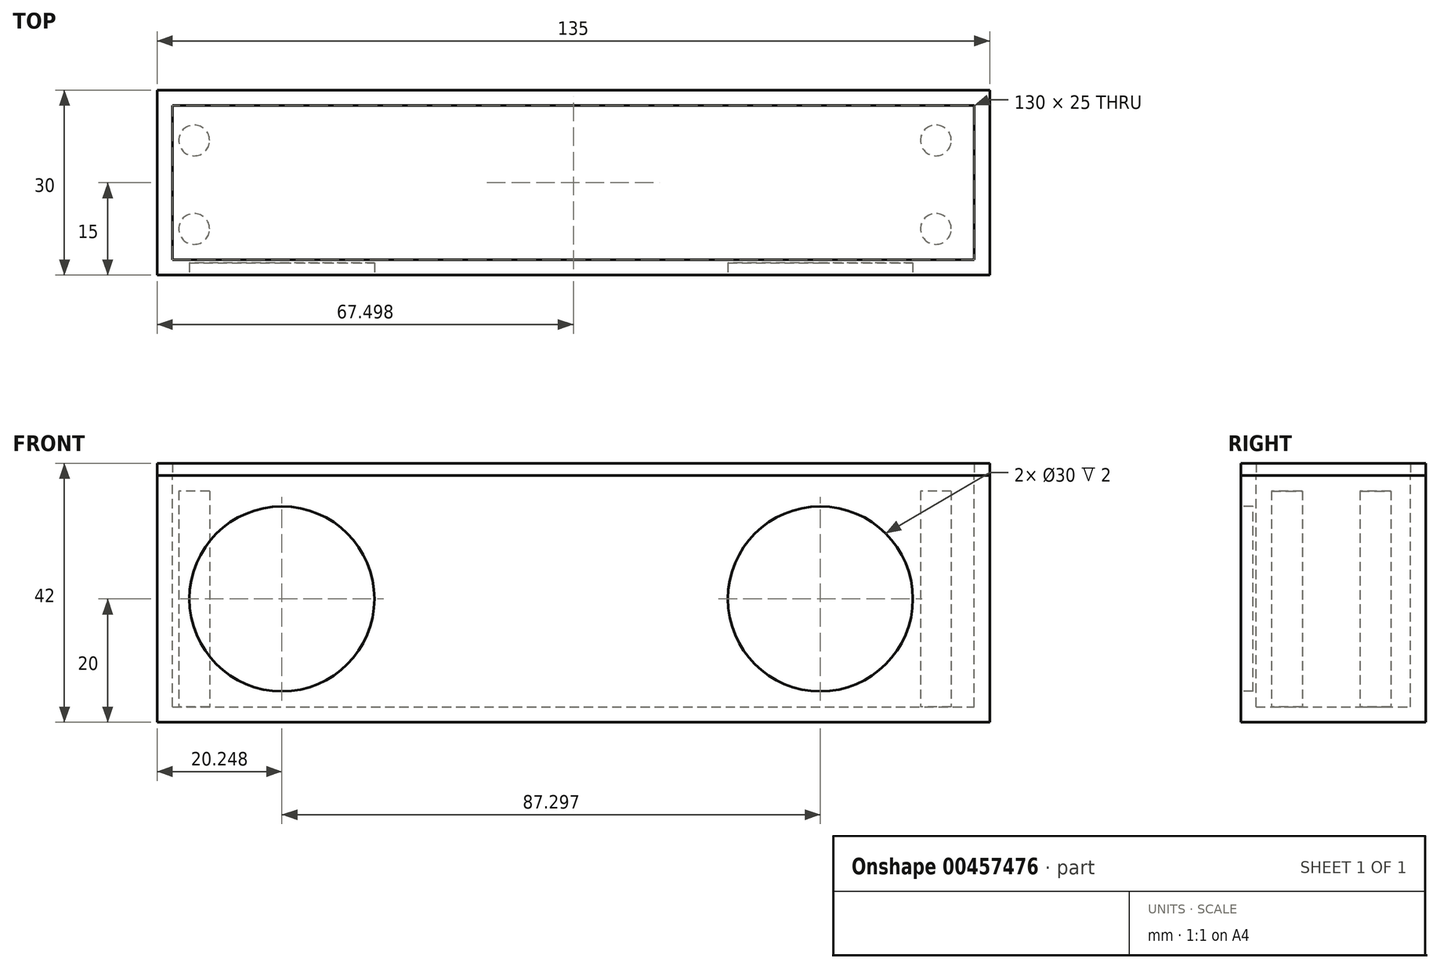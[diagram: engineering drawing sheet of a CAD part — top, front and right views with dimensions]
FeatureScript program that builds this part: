
annotation { "Feature Type Name" : "Feature", "Feature Type Description" : "" }
export const myFeature = defineFeature(function(context is Context, id is Id, definition is map)
    precondition{}
    {
        {
            var Q0;
            Q0=qCreatedBy(makeId("Front.planeOp"),FACE);
            var sketch = newSketch(context, id + "F0", { "sketchPlane" : qUnion([Q0])});
            skLineSegment(sketch, "E0.bottom", {"start": v(-68.08, 0) * mm, "end": v(66.92, 0) * mm});
            skLineSegment(sketch, "E0.top", {"start": v(-68.08, 30) * mm, "end": v(66.92, 30) * mm});
            skLineSegment(sketch, "E0.left", {"start": v(-68.08, 0) * mm, "end": v(-68.08, 30) * mm});
            skLineSegment(sketch, "E0.right", {"start": v(66.92, 0) * mm, "end": v(66.92, 30) * mm});
            skSolve(sketch);
        }
        {
            var Q0;
            Q0=makeQuery(id+"F0.imprint","IMPRINT",FACE,{"disambiguationData":[TD([[makeQuery(id+"F0.imprint","IMPRINT",EDGE,{"derivedFrom":sQuery(id+"F0.wireOp",EDGE,"E0.bottom")}),1.0]])]});
            extrude(context, id + "F1", {"entities" : qUnion([Q0]), "depth" : 30 * mm});
        }
        {
            var Q0;
            Q0=makeQuery(id+"F1.opExtrude","SWEPT_FACE",FACE,{"disambiguationData":[OSD([sQuery(id+"F0.wireOp",EDGE,"E0.top")])]});
            shell(context, id + "F2", {"entities" : qUnion([Q0]), "thickness" : 2.5 * mm});
        }
        {
            var Q0;
            Q0=makeQuery(id+"F2.opShell","OFFSET_FACE",FACE,{"disambiguationData":[OSD([sQuery(id+"F0.wireOp",EDGE,"E0.bottom")])]});
            var sketch = newSketch(context, id + "F3", { "sketchPlane" : qUnion([Q0])});
            skCircle(sketch, "E1", {"center": v(-62.07, -8.15) * mm, "radius": 2.5 * mm});
            skCircle(sketch, "E2", {"center": v(58.19, -8.15) * mm, "radius": 2.5 * mm});
            skCircle(sketch, "E3", {"center": v(58.19, -22.5) * mm, "radius": 2.5 * mm});
            skCircle(sketch, "E4", {"center": v(-62.07, -22.5) * mm, "radius": 2.5 * mm});
            skSolve(sketch);
        }
        {
            var Q0;
            Q0=makeQuery(id+"F3.imprint","IMPRINT",FACE,{"disambiguationData":[TD([[makeQuery(id+"F3.imprint","IMPRINT",EDGE,{"derivedFrom":sQuery(id+"F3.wireOp",EDGE,"E1")}),1.0]])]});
            var Q1;
            Q1=makeQuery(id+"F3.imprint","IMPRINT",FACE,{"disambiguationData":[TD([[makeQuery(id+"F3.imprint","IMPRINT",EDGE,{"derivedFrom":sQuery(id+"F3.wireOp",EDGE,"E4")}),1.0]])]});
            var Q2;
            Q2=makeQuery(id+"F3.imprint","IMPRINT",FACE,{"disambiguationData":[TD([[makeQuery(id+"F3.imprint","IMPRINT",EDGE,{"derivedFrom":sQuery(id+"F3.wireOp",EDGE,"E3")}),1.0]])]});
            var Q3;
            Q3=makeQuery(id+"F3.imprint","IMPRINT",FACE,{"disambiguationData":[TD([[makeQuery(id+"F3.imprint","IMPRINT",EDGE,{"derivedFrom":sQuery(id+"F3.wireOp",EDGE,"E2")}),1.0]])]});
            extrude(context, id + "F4", {"entities" : qUnion([Q0, Q1, Q2, Q3]), "operationType" : NewBodyOperationType.ADD, "depth" : 35 * mm});
        }
        {
            var Q0;
            Q0=makeQuery(id+"F1.opExtrude","SWEPT_FACE",FACE,{"disambiguationData":[OSD([sQuery(id+"F0.wireOp",EDGE,"E0.top")])]});
            extrude(context, id + "F5", {"entities" : qUnion([Q0]), "operationType" : NewBodyOperationType.ADD, "depth" : 5 * mm});
        }
        {
            var Q0;
            Q0=makeQuery(id+"F5.opExtrude","CAP_FACE",FACE,{"disambiguationData":[OSD([sQuery(id+"F0.wireOp",EDGE,"E0.top")])],"isStart":false});
            extrude(context, id + "F6", {"entities" : qUnion([Q0]), "operationType" : NewBodyOperationType.ADD, "depth" : 5 * mm});
        }
        {
            var Q0;
            Q0=makeQuery(id+"F6.opExtrude","CAP_FACE",FACE,{"disambiguationData":[OSD([sQuery(id+"F0.wireOp",EDGE,"E0.top")])],"isStart":false});
            var sketch = newSketch(context, id + "F7", { "sketchPlane" : qUnion([Q0])});
            skLineSegment(sketch, "E5.bottom", {"start": v(-68.08, -30) * mm, "end": v(66.92, -30) * mm});
            skLineSegment(sketch, "E5.top", {"start": v(-68.08, 0) * mm, "end": v(66.92, 0) * mm});
            skLineSegment(sketch, "E5.left", {"start": v(-68.08, -30) * mm, "end": v(-68.08, 0) * mm});
            skLineSegment(sketch, "E5.right", {"start": v(66.92, -30) * mm, "end": v(66.92, 0) * mm});
            skSolve(sketch);
        }
        {
            var Q0;
            {var subQ1=sQuery(id+"F0.wireOp",EDGE,"E0.top");Q0=makeQuery(id+"F7.imprint","IMPRINT",FACE,{"disambiguationData":[TD([[makeQuery(id+"F7.imprint","IMPRINT",EDGE,{"derivedFrom":makeQuery(id+"F6.opExtrude","CAP_EDGE",EDGE,{"disambiguationData":[OSD([subQ1]),TDD([makeQuery(id+"F5.opExtrude","CAP_EDGE",EDGE,{"disambiguationData":[OSD([subQ1]),TDD([makeQuery(id+"F2.opShell","OFFSET_EDGE",EDGE,{"disambiguationData":[OSD([subQ1]),TDD([makeQuery(id+"F1.opExtrude","CAP_EDGE",EDGE,{"disambiguationData":[OSD([subQ1])],"isStart":true})])]})])],"isStart":false})])],"isStart":false})}),-1.0]])]});}
            extrude(context, id + "F8", {"entities" : qUnion([Q0]), "depth" : 2 * mm});
        }
        {
            var Q0;
            Q0=makeQuery(id+"F6.opExtrude","CAP_FACE",FACE,{"disambiguationData":[OSD([sQuery(id+"F0.wireOp",EDGE,"E0.top")])],"isStart":false});
            extrude(context, id + "F9", {"entities" : qUnion([Q0]), "depth" : 2 * mm});
        }
        {
            var Q0;
            {var subQ0=sQuery(id+"F0.wireOp",EDGE,"E0.top");var subQ1=makeQuery(id+"F1.opExtrude","CAP_EDGE",EDGE,{"disambiguationData":[OSD([subQ0])],"isStart":false});Q0=makeQuery(id+"F6.boolean.opBoolean","MERGE",FACE,{"derivedFrom":[makeQuery(id+"F5.boolean.opBoolean","MERGE",FACE,{"derivedFrom":[makeQuery(id+"F1.opExtrude","CAP_FACE",FACE,{"disambiguationData":[OSD([sQuery(id+"F0.wireOp",EDGE,"E0.bottom"),subQ0,sQuery(id+"F0.wireOp",EDGE,"E0.left"),sQuery(id+"F0.wireOp",EDGE,"E0.right")])],"isStart":false}),makeQuery(id+"F5.opExtrude","SWEPT_FACE",FACE,{"disambiguationData":[OSD([subQ0]),TDD([subQ1])]})]}),makeQuery(id+"F6.opExtrude","SWEPT_FACE",FACE,{"disambiguationData":[OSD([subQ0]),TDD([makeQuery(id+"F5.opExtrude","CAP_EDGE",EDGE,{"disambiguationData":[OSD([subQ0]),TDD([subQ1])],"isStart":false})])]})]});}
            var sketch = newSketch(context, id + "F10", { "sketchPlane" : qUnion([Q0])});
            skCircle(sketch, "E6", {"center": v(-47.83, 20) * mm, "radius": 15 * mm});
            skPoint(sketch, "E6.centerSnap0", {"position": v(-68.08, 20) * mm});
            skCircle(sketch, "E7", {"center": v(39.46, 20) * mm, "radius": 15 * mm});
            skPoint(sketch, "E7.centerSnap0", {"position": v(66.92, 20) * mm});
            skSolve(sketch);
        }
        {
            var Q0;
            Q0=makeQuery(id+"F10.imprint","IMPRINT",FACE,{"disambiguationData":[TD([[makeQuery(id+"F10.imprint","IMPRINT",EDGE,{"derivedFrom":sQuery(id+"F10.wireOp",EDGE,"E6")}),1.0]])]});
            var Q1;
            Q1=makeQuery(id+"F10.imprint","IMPRINT",FACE,{"disambiguationData":[TD([[makeQuery(id+"F10.imprint","IMPRINT",EDGE,{"derivedFrom":sQuery(id+"F10.wireOp",EDGE,"E7")}),1.0]])]});
            extrude(context, id + "F11", {"entities" : qUnion([Q0, Q1]), "operationType" : NewBodyOperationType.REMOVE, "oppositeDirection" : true, "depth" : 2 * mm});
        }
    });
